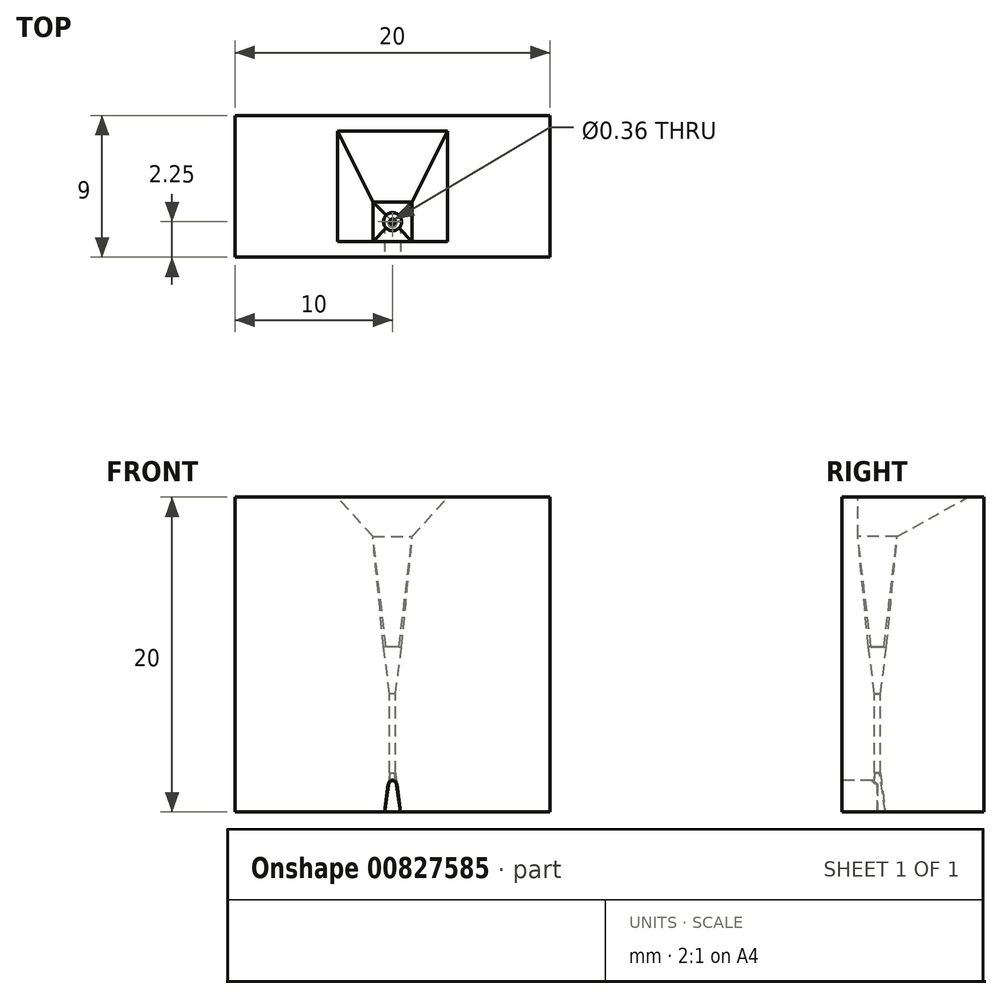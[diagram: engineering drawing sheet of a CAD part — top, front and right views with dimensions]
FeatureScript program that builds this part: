
annotation { "Feature Type Name" : "Feature", "Feature Type Description" : "" }
export const myFeature = defineFeature(function(context is Context, id is Id, definition is map)
    precondition{}
    {
        {
            var Q0;
            Q0=qCreatedBy(makeId("Top.planeOp"),FACE);
            var sketch = newSketch(context, id + "F0", { "sketchPlane" : qUnion([Q0])});
            skLineSegment(sketch, "E0.bottom", {"start": v(-10, 4.5) * mm, "end": v(10, 4.5) * mm});
            skLineSegment(sketch, "E0.top", {"start": v(-10, -4.5) * mm, "end": v(10, -4.5) * mm});
            skLineSegment(sketch, "E0.left", {"start": v(-10, 4.5) * mm, "end": v(-10, -4.5) * mm});
            skLineSegment(sketch, "E0.right", {"start": v(10, 4.5) * mm, "end": v(10, -4.5) * mm});
            skLineSegment(sketch, "E1", {"start": v(0, 4.5) * mm, "end": v(0, -4.5) * mm, "construction": true});
            skLineSegment(sketch, "E2", {"start": v(10, 0) * mm, "end": v(-10, 0) * mm, "construction": true});
            skSolve(sketch);
        }
        {
            var Q0;
            Q0=makeQuery(id+"F0.imprint","IMPRINT",FACE,{"disambiguationData":[TD([[makeQuery(id+"F0.imprint","IMPRINT",EDGE,{"derivedFrom":sQuery(id+"F0.wireOp",EDGE,"E0.bottom")}),-1.0]])]});
            extrude(context, id + "F1", {"entities" : qUnion([Q0]), "depth" : 20 * mm, "offsetDistance" : 25 * mm});
        }
        {
            var Q0;
            Q0=makeQuery(id+"F1.opExtrude","CAP_FACE",FACE,{"disambiguationData":[OSD([sQuery(id+"F0.wireOp",EDGE,"E0.bottom"),sQuery(id+"F0.wireOp",EDGE,"E0.top"),sQuery(id+"F0.wireOp",EDGE,"E0.left"),sQuery(id+"F0.wireOp",EDGE,"E0.right")])],"isStart":false});
            var sketch = newSketch(context, id + "F2", { "sketchPlane" : qUnion([Q0])});
            skCircle(sketch, "E3", {"center": v(0, 0) * mm, "radius": 3.5 * mm, "construction": true});
            skLineSegment(sketch, "E4.bottom", {"start": v(-3.5, 3.5) * mm, "end": v(3.5, 3.5) * mm});
            skLineSegment(sketch, "E4.top", {"start": v(-3.5, -3.5) * mm, "end": v(3.5, -3.5) * mm});
            skLineSegment(sketch, "E4.left", {"start": v(-3.5, 3.5) * mm, "end": v(-3.5, -3.5) * mm});
            skLineSegment(sketch, "E4.right", {"start": v(3.5, 3.5) * mm, "end": v(3.5, -3.5) * mm});
            skSolve(sketch);
        }
        {
            var Q0;
            Q0=makeQuery(id+"F1.opExtrude","CAP_FACE",FACE,{"disambiguationData":[OSD([sQuery(id+"F0.wireOp",EDGE,"E0.bottom"),sQuery(id+"F0.wireOp",EDGE,"E0.top"),sQuery(id+"F0.wireOp",EDGE,"E0.left"),sQuery(id+"F0.wireOp",EDGE,"E0.right")])],"isStart":false});
            cPlane(context, id + "F3", {"entities" : qUnion([Q0]), "cplaneType" : CPlaneType.OFFSET, "offset" : 2.5 * mm, "oppositeDirection" : true, "width" : 150 * mm, "height" : 150 * mm});
        }
        {
            var Q0;
            Q0=qCreatedBy(id+"F3.planeOp",FACE);
            var sketch = newSketch(context, id + "F4", { "sketchPlane" : qUnion([Q0])});
            skCircle(sketch, "E5", {"center": v(0, -2.25) * mm, "radius": 1.25 * mm, "construction": true});
            skLineSegment(sketch, "E6", {"start": v(0, 0) * mm, "end": v(0, -4.5) * mm, "construction": true});
            skLineSegment(sketch, "E7.bottom", {"start": v(-1.25, -1) * mm, "end": v(1.25, -1) * mm});
            skLineSegment(sketch, "E7.top", {"start": v(-1.25, -3.5) * mm, "end": v(1.25, -3.5) * mm});
            skLineSegment(sketch, "E7.left", {"start": v(-1.25, -1) * mm, "end": v(-1.25, -3.5) * mm});
            skLineSegment(sketch, "E7.right", {"start": v(1.25, -1) * mm, "end": v(1.25, -3.5) * mm});
            skSolve(sketch);
        }
        {
            var Q0;
            Q0=qCreatedBy(makeId("Right.planeOp"),FACE);
            var sketch = newSketch(context, id + "F5", { "sketchPlane" : qUnion([Q0])});
            skLineSegment(sketch, "E8", {"start": v(-3.5, 20) * mm, "end": v(-3.5, 17.5) * mm});
            skSolve(sketch);
        }
        {
            var Q0;
            Q0=qCreatedBy(id+"F3.planeOp",FACE);
            cPlane(context, id + "F6", {"entities" : qUnion([Q0]), "cplaneType" : CPlaneType.OFFSET, "offset" : 7 * mm, "oppositeDirection" : true, "width" : 150 * mm, "height" : 150 * mm});
        }
        {
            var Q0;
            Q0=qCreatedBy(id+"F6.planeOp",FACE);
            var sketch = newSketch(context, id + "F7", { "sketchPlane" : qUnion([Q0])});
            skCircle(sketch, "E9", {"center": v(0, -2.25) * mm, "radius": 0.58 * mm});
            skSolve(sketch);
        }
        {
            var Q1;
            Q1 = qSketchRegion(id + "F4", true);
            var Q2;
            Q2 = qSketchRegion(id + "F2", true);
            var Q3;
            Q3=sQuery(id+"F4.wireOp",EDGE,"E5");
            var Q4;
            Q4=sQuery(id+"F2.wireOp",EDGE,"E3");
            var Q5;
            Q5=sQuery(id+"F5.wireOp",EDGE,"E8");
            loft(context, id + "F8", {"operationType" : NewBodyOperationType.REMOVE, "addGuides" : true, "sheetProfilesArray" : [{ "sheetProfileEntities" : qUnion([Q1]) }, { "sheetProfileEntities" : qUnion([Q2]) }], "wireProfilesArray" : [{ "wireProfileEntities" : qUnion([Q3]) }, { "wireProfileEntities" : qUnion([Q4]) }], "guidesArray" : [{ "guideEntities" : qUnion([Q5]), "guideDerivativeType" : LoftGuideDerivativeType.DEFAULT, "guideDerivativeMagnitude" : 1 }]});
        }
        {
            var Q1;
            Q1 = qSketchRegion(id + "F7", true);
            var Q2;
            Q2 = qSketchRegion(id + "F4", true);
            loft(context, id + "F9", {"operationType" : NewBodyOperationType.REMOVE, "sheetProfilesArray" : [{ "sheetProfileEntities" : qUnion([Q1]) }, { "sheetProfileEntities" : qUnion([Q2]) }]});
        }
        {
            var Q0;
            Q0=qCreatedBy(makeId("Right.planeOp"),FACE);
            var sketch = newSketch(context, id + "F10", { "sketchPlane" : qUnion([Q0])});
            skLineSegment(sketch, "E10", {"start": v(-2.43, 7.5) * mm, "end": v(-2.43, 2.5) * mm});
            skLineSegment(sketch, "E11", {"start": v(-2.43, 7.5) * mm, "end": v(-2.25, 7.5) * mm, "construction": true});
            skLineSegment(sketch, "E12", {"start": v(-2.43, 2.5) * mm, "end": v(-2.25, 2.5) * mm});
            skLineSegment(sketch, "E13", {"start": v(-2.43, 7.5) * mm, "end": v(-2.83, 10.5) * mm});
            skPoint(sketch, "E14", {"position": v(-2.25, 10.5) * mm});
            skLineSegment(sketch, "E15", {"start": v(-2.25, 10.5) * mm, "end": v(-2.25, 2.5) * mm});
            skLineSegment(sketch, "E16", {"start": v(-2.83, 10.5) * mm, "end": v(-2.25, 10.5) * mm});
            skLineSegment(sketch, "E17", {"start": v(0, 0) * mm, "end": v(-4.5, 0) * mm, "construction": true});
            skLineSegment(sketch, "E18", {"start": v(-2.25, 10.5) * mm, "end": v(-2.25, 0) * mm, "construction": true});
            skSolve(sketch);
        }
        {
            var Q0;
            Q0=qCreatedBy(makeId("Right.planeOp"),FACE);
            var sketch = newSketch(context, id + "F11", { "sketchPlane" : qUnion([Q0])});
            skLineSegment(sketch, "E19", {"start": v(-2.25, -2.65) * mm, "end": v(-2.25, 31.53) * mm});
            skSolve(sketch);
        }
        {
            var Q0;
            Q0=makeQuery(id+"F10.imprint","IMPRINT",FACE,{"disambiguationData":[TD([[makeQuery(id+"F10.imprint","IMPRINT",EDGE,{"derivedFrom":sQuery(id+"F10.wireOp",EDGE,"E10")}),1.0]])]});
            var Q1;
            Q1=sQuery(id+"F11.wireOp",EDGE,"E19");
            revolve(context, id + "F12", {"operationType" : NewBodyOperationType.REMOVE, "surfaceOperationType" : NewSurfaceOperationType.NEW, "entities" : qUnion([Q0]), "axis" : qUnion([Q1]), "revolveType" : RevolveType.ONE_DIRECTION, "oppositeDirection" : true, "angle" : 360 * degree});
        }
        {
            var Q0;
            Q0=makeQuery(id+"F1.opExtrude","CAP_FACE",FACE,{"disambiguationData":[OSD([sQuery(id+"F0.wireOp",EDGE,"E0.bottom"),sQuery(id+"F0.wireOp",EDGE,"E0.top"),sQuery(id+"F0.wireOp",EDGE,"E0.left"),sQuery(id+"F0.wireOp",EDGE,"E0.right")])],"isStart":true});
            var sketch = newSketch(context, id + "F13", { "sketchPlane" : qUnion([Q0])});
            skLineSegment(sketch, "E20.bottom", {"start": v(0.5, 1.75) * mm, "end": v(-0.5, 1.75) * mm});
            skLineSegment(sketch, "E20.top", {"start": v(0.5, 2.75) * mm, "end": v(-0.5, 2.75) * mm});
            skLineSegment(sketch, "E20.left", {"start": v(0.5, 1.75) * mm, "end": v(0.5, 2.75) * mm});
            skLineSegment(sketch, "E20.right", {"start": v(-0.5, 1.75) * mm, "end": v(-0.5, 2.75) * mm});
            skPoint(sketch, "E20.middle", {"position": v(0, 2.25) * mm});
            skSolve(sketch);
        }
        {
            var Q1;
            Q1 = qSketchRegion(id + "F13", true);
            var Q2;
            Q2=makeQuery(id+"F12.boolean.opBoolean","COPY",FACE,{"derivedFrom":makeQuery(id+"F12.opRevolve","SWEPT_FACE",FACE,{"disambiguationData":[OSD([sQuery(id+"F10.wireOp",EDGE,"E12")])]})});
            loft(context, id + "F14", {"operationType" : NewBodyOperationType.REMOVE, "sheetProfilesArray" : [{ "sheetProfileEntities" : qUnion([Q1]) }, { "sheetProfileEntities" : qUnion([Q2]) }]});
        }
        {
            var Q0;
            Q0=makeQuery(id+"F1.opExtrude","SWEPT_FACE",FACE,{"disambiguationData":[OSD([sQuery(id+"F0.wireOp",EDGE,"E0.top")])]});
            var sketch = newSketch(context, id + "F15", { "sketchPlane" : qUnion([Q0])});
            skLineSegment(sketch, "E21", {"start": v(-0.18, 2.5) * mm, "end": v(0.18, 2.5) * mm, "construction": true});
            skLineSegment(sketch, "E22", {"start": v(-0.5, 0) * mm, "end": v(0.5, 0) * mm});
            skLineSegment(sketch, "E23", {"start": v(-0.18, 2.5) * mm, "end": v(-0.24, 2) * mm, "construction": true});
            skLineSegment(sketch, "E24", {"start": v(0.18, 2.5) * mm, "end": v(0.24, 2) * mm, "construction": true});
            skLineSegment(sketch, "E25", {"start": v(-0.24, 2) * mm, "end": v(0.24, 2) * mm, "construction": true});
            skArc(sketch, "E26", {"start": v(0.27, 1.76) * mm, "mid": v(0, 2) * mm, "end": v(-0.27, 1.76) * mm});
            skLineSegment(sketch, "E27", {"start": v(-0.18, 2.5) * mm, "end": v(-0.5, 0) * mm, "construction": true});
            skLineSegment(sketch, "E28", {"start": v(0.18, 2.5) * mm, "end": v(0.5, 0) * mm, "construction": true});
            skLineSegment(sketch, "E29", {"start": v(-0.5, 0) * mm, "end": v(-0.27, 1.76) * mm});
            skLineSegment(sketch, "E30", {"start": v(0.5, 0) * mm, "end": v(0.27, 1.76) * mm});
            skSolve(sketch);
        }
        {
            var Q0;
            Q0=makeQuery(id+"F15.imprint","IMPRINT",FACE,{"disambiguationData":[TD([[makeQuery(id+"F15.imprint","IMPRINT",EDGE,{"derivedFrom":sQuery(id+"F15.wireOp",EDGE,"E22")}),1.0]])]});
            extrude(context, id + "F16", {"entities" : qUnion([Q0]), "operationType" : NewBodyOperationType.REMOVE, "oppositeDirection" : true, "depth" : 2.25 * mm, "offsetDistance" : 25 * mm});
        }
        {
            var Q0;
            Q0=makeQuery(id+"F16.boolean.opBoolean","COPY",EDGE,{"derivedFrom":makeQuery(id+"F16.opExtrude","CAP_EDGE",EDGE,{"disambiguationData":[OSD([sQuery(id+"F15.wireOp",EDGE,"E26")])],"isStart":true})});
            var Q1;
            {var subQ0=sQuery(id+"F13.wireOp",EDGE,"E20.left");var subQ1=sQuery(id+"F13.wireOp",EDGE,"E20.right");var subQ2=sQuery(id+"F13.wireOp",EDGE,"E20.top");var subQ3=sQuery(id+"F13.wireOp",EDGE,"E20.bottom");var subQ4=sQuery(id+"F10.wireOp",EDGE,"E12");var subQ5=sQuery(id+"F10.wireOp",EDGE,"E10");Q1=makeQuery(id+"F16.boolean.opBoolean","INTERSECT",EDGE,{"derivedFrom":[makeQuery(id+"F14.boolean.opBoolean","COPY",FACE,{"derivedFrom":makeQuery(id+"F14.opLoft","SWEPT_FACE",FACE,{"disambiguationData":[OSD([subQ5,subQ4,subQ3,subQ2,subQ0,subQ1]),TDD([makeQuery(id+"F12.boolean.opBoolean","COPY",EDGE,{"derivedFrom":makeQuery(id+"F12.opRevolve","SWEPT_EDGE",EDGE,{"disambiguationData":[OSD([subQ5,subQ4])]})}),makeQuery(id+"F13.imprint","INTERSECT",VERTEX,{"derivedFrom":[subQ3,subQ0]}),makeQuery(id+"F13.imprint","INTERSECT",VERTEX,{"derivedFrom":[subQ2,subQ0]}),makeQuery(id+"F13.imprint","INTERSECT",VERTEX,{"derivedFrom":[subQ2,subQ1]}),makeQuery(id+"F13.imprint","IMPRINT",EDGE,{"derivedFrom":subQ0})])]})}),makeQuery(id+"F16.opExtrude","SWEPT_FACE",FACE,{"disambiguationData":[OSD([sQuery(id+"F15.wireOp",EDGE,"E26")])]})]});}
            var Q2;
            {var subQ0=sQuery(id+"F13.wireOp",EDGE,"E20.top");var subQ1=sQuery(id+"F13.wireOp",EDGE,"E20.right");var subQ2=sQuery(id+"F13.wireOp",EDGE,"E20.left");var subQ3=sQuery(id+"F13.wireOp",EDGE,"E20.bottom");var subQ4=sQuery(id+"F10.wireOp",EDGE,"E12");var subQ5=sQuery(id+"F10.wireOp",EDGE,"E10");Q2=makeQuery(id+"F16.boolean.opBoolean","INTERSECT",EDGE,{"derivedFrom":[makeQuery(id+"F14.boolean.opBoolean","COPY",FACE,{"derivedFrom":makeQuery(id+"F14.opLoft","SWEPT_FACE",FACE,{"disambiguationData":[OSD([subQ5,subQ4,subQ3,subQ0,subQ2,subQ1]),TDD([makeQuery(id+"F12.boolean.opBoolean","COPY",EDGE,{"derivedFrom":makeQuery(id+"F12.opRevolve","SWEPT_EDGE",EDGE,{"disambiguationData":[OSD([subQ5,subQ4])]})}),makeQuery(id+"F13.imprint","INTERSECT",VERTEX,{"derivedFrom":[subQ3,subQ1]}),makeQuery(id+"F13.imprint","INTERSECT",VERTEX,{"derivedFrom":[subQ0,subQ2]}),makeQuery(id+"F13.imprint","INTERSECT",VERTEX,{"derivedFrom":[subQ0,subQ1]}),makeQuery(id+"F13.imprint","IMPRINT",EDGE,{"derivedFrom":subQ0})])]})}),makeQuery(id+"F16.opExtrude","SWEPT_FACE",FACE,{"disambiguationData":[OSD([sQuery(id+"F15.wireOp",EDGE,"E26")])]})]});}
            var Q3;
            {var subQ0=sQuery(id+"F13.wireOp",EDGE,"E20.right");var subQ1=sQuery(id+"F13.wireOp",EDGE,"E20.top");var subQ2=sQuery(id+"F13.wireOp",EDGE,"E20.bottom");var subQ3=sQuery(id+"F13.wireOp",EDGE,"E20.left");var subQ4=sQuery(id+"F10.wireOp",EDGE,"E12");var subQ5=sQuery(id+"F10.wireOp",EDGE,"E10");Q3=makeQuery(id+"F16.boolean.opBoolean","INTERSECT",EDGE,{"derivedFrom":[makeQuery(id+"F14.boolean.opBoolean","COPY",FACE,{"derivedFrom":makeQuery(id+"F14.opLoft","SWEPT_FACE",FACE,{"disambiguationData":[OSD([subQ5,subQ4,subQ2,subQ1,subQ3,subQ0]),TDD([makeQuery(id+"F12.boolean.opBoolean","COPY",EDGE,{"derivedFrom":makeQuery(id+"F12.opRevolve","SWEPT_EDGE",EDGE,{"disambiguationData":[OSD([subQ5,subQ4])]})}),makeQuery(id+"F13.imprint","INTERSECT",VERTEX,{"derivedFrom":[subQ2,subQ3]}),makeQuery(id+"F13.imprint","INTERSECT",VERTEX,{"derivedFrom":[subQ2,subQ0]}),makeQuery(id+"F13.imprint","INTERSECT",VERTEX,{"derivedFrom":[subQ1,subQ0]}),makeQuery(id+"F13.imprint","IMPRINT",EDGE,{"derivedFrom":subQ0})])]})}),makeQuery(id+"F16.opExtrude","SWEPT_FACE",FACE,{"disambiguationData":[OSD([sQuery(id+"F15.wireOp",EDGE,"E26")])]})]});}
            fillet(context, id + "F17", {"entities" : qUnion([Q0, Q1, Q2, Q3]), "radius" : 0.1 * mm, "tangentPropagation" : true, "allowEdgeOverflow" : false});
        }
    });
